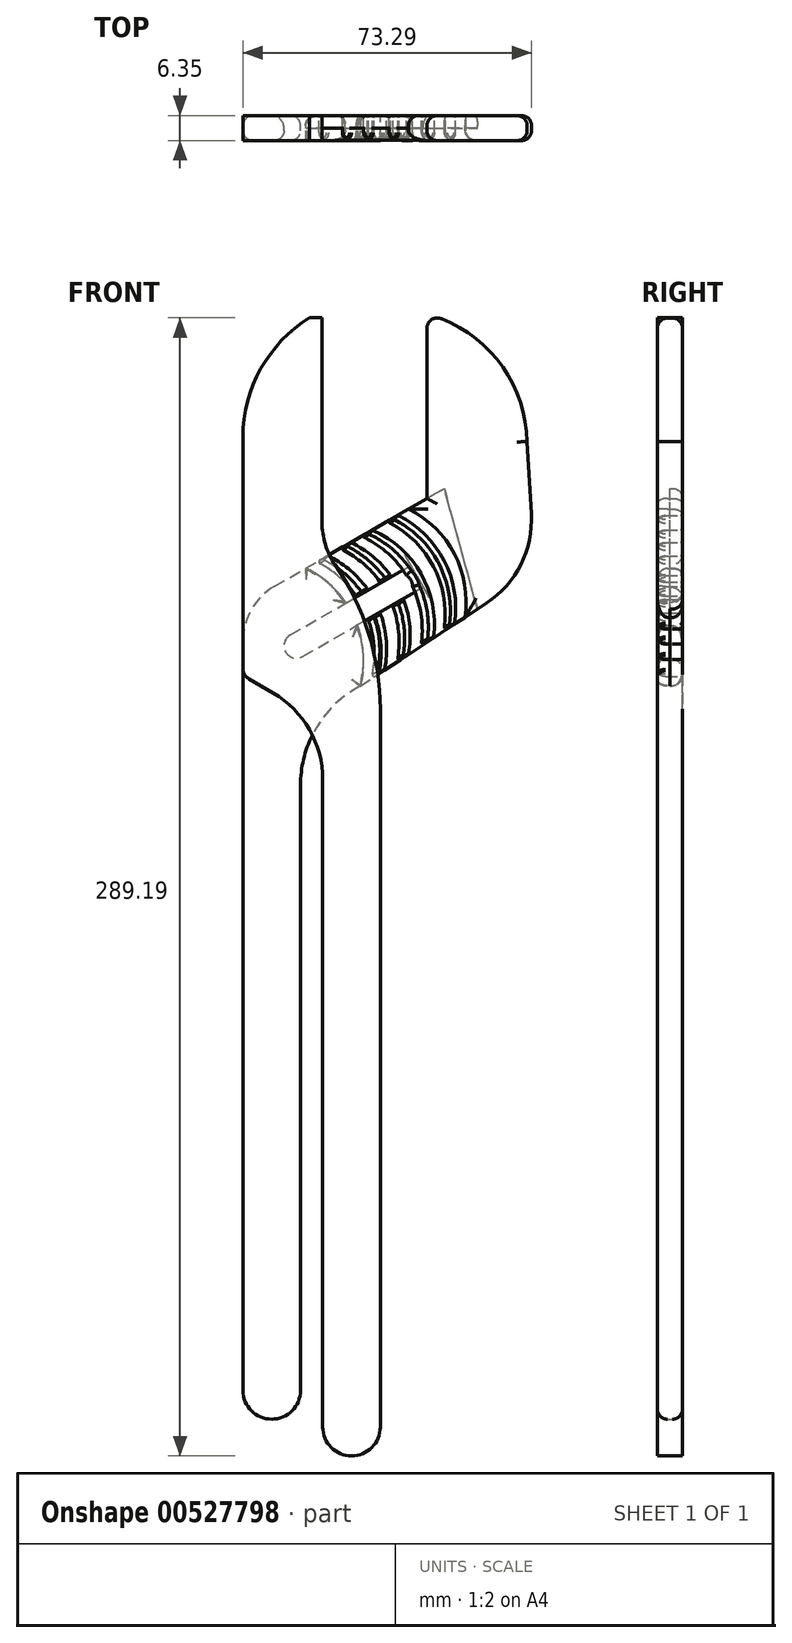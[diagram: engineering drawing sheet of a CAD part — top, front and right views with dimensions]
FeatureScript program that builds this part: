
annotation { "Feature Type Name" : "Feature", "Feature Type Description" : "" }
export const myFeature = defineFeature(function(context is Context, id is Id, definition is map)
    precondition{}
    {
        {
            var Q0;
            Q0=qCreatedBy(makeId("Front.planeOp"),FACE);
            var sketch = newSketch(context, id + "F0", { "sketchPlane" : qUnion([Q0])});
            skLineSegment(sketch, "E0", {"start": v(-2.94, 1.56) * mm, "end": v(-2.94, 179.72) * mm});
            skLineSegment(sketch, "E1", {"start": v(11.68, -10.78) * mm, "end": v(11.68, 143.04) * mm});
            skLineSegment(sketch, "E2", {"start": v(5, 193.46) * mm, "end": v(43.8, 215.87) * mm});
            skLineSegment(sketch, "E3", {"start": v(43.8, 261.68) * mm, "end": v(43.8, 215.87) * mm});
            skPoint(sketch, "E4.visualSharp", {"position": v(11.68, 160.66) * mm});
            skPoint(sketch, "E5.visualSharp", {"position": v(71.16, 197.3) * mm});
            skPoint(sketch, "E6.visualSharp", {"position": v(-2.94, 188.88) * mm});
            skArc(sketch, "E6.filletArc", {"start": v(5, 193.46) * mm, "mid": v(-0.82, 187.65) * mm, "end": v(-2.94, 179.72) * mm});
            skPoint(sketch, "E7.startSnap0", {"position": v(-0.82, 187.65) * mm});
            skLineSegment(sketch, "E8", {"start": v(-2.94, 1.56) * mm, "end": v(-2.94, -10.78) * mm});
            skLineSegment(sketch, "E9", {"start": v(26.87, 168.17) * mm, "end": v(58.9, 189.24) * mm});
            skArc(sketch, "E10", {"start": v(69.24, 230.28) * mm, "mid": v(62.94, 249.4) * mm, "end": v(46.97, 261.68) * mm});
            skLineSegment(sketch, "E11", {"start": v(43.8, 261.68) * mm, "end": v(46.97, 261.68) * mm});
            skLineSegment(sketch, "E12", {"start": v(69.24, 230.28) * mm, "end": v(70.3, 211.93) * mm});
            skArc(sketch, "E13.filletArc", {"start": v(58.9, 189.24) * mm, "mid": v(67.64, 199.06) * mm, "end": v(70.3, 211.93) * mm});
            skLineSegment(sketch, "E14", {"start": v(12.24, 175.65) * mm, "end": v(38.54, 190.84) * mm});
            skLineSegment(sketch, "E15", {"start": v(9.07, 181.15) * mm, "end": v(35.37, 196.34) * mm});
            skArc(sketch, "E16", {"start": v(-2.94, -10.78) * mm, "mid": v(4.37, -18.1) * mm, "end": v(11.68, -10.78) * mm});
            skArc(sketch, "E17", {"start": v(53.42, 185.63) * mm, "mid": v(50.77, 201.74) * mm, "end": v(39.08, 213.14) * mm});
            skArc(sketch, "E18", {"start": v(50.76, 183.88) * mm, "mid": v(48.13, 200.1) * mm, "end": v(36.33, 211.55) * mm});
            skArc(sketch, "E19", {"start": v(48.1, 182.14) * mm, "mid": v(45.48, 198.47) * mm, "end": v(33.58, 209.97) * mm});
            skArc(sketch, "E20", {"start": v(45.46, 180.4) * mm, "mid": v(42.28, 196.73) * mm, "end": v(29.9, 207.84) * mm});
            skArc(sketch, "E21", {"start": v(42.28, 178.3) * mm, "mid": v(42.34, 186.06) * mm, "end": v(40.13, 193.49) * mm});
            skPoint(sketch, "E21.startSnap0", {"position": v(42.28, 196.73) * mm});
            skArc(sketch, "E22", {"start": v(39.1, 176.22) * mm, "mid": v(39.42, 183.4) * mm, "end": v(37.77, 190.4) * mm});
            skArc(sketch, "E23", {"start": v(36.2, 174.3) * mm, "mid": v(36.62, 181.63) * mm, "end": v(35, 188.79) * mm});
            skArc(sketch, "E24", {"start": v(29.65, 170) * mm, "mid": v(30.36, 177.67) * mm, "end": v(28.8, 185.22) * mm});
            skArc(sketch, "E25", {"start": v(26.87, 168.17) * mm, "mid": v(27.65, 175.97) * mm, "end": v(26.08, 183.64) * mm});
            skArc(sketch, "E26", {"start": v(9.07, 181.15) * mm, "mid": v(7.9, 176.81) * mm, "end": v(12.24, 175.65) * mm});
            skArc(sketch, "E27", {"start": v(38.54, 190.84) * mm, "mid": v(39.7, 195.17) * mm, "end": v(35.37, 196.34) * mm});
            skArc(sketch, "E28.trimOffspring", {"start": v(23.18, 189.3) * mm, "mid": v(18.69, 194.37) * mm, "end": v(13.04, 198.11) * mm});
            skArc(sketch, "E29.trimOffspring", {"start": v(25.92, 190.88) * mm, "mid": v(21.43, 195.95) * mm, "end": v(15.8, 199.7) * mm});
            skArc(sketch, "E30.trimOffspring", {"start": v(32.02, 194.4) * mm, "mid": v(27.44, 199.44) * mm, "end": v(21.72, 203.12) * mm});
            skArc(sketch, "E31.trimOffspring", {"start": v(34.77, 196) * mm, "mid": v(30.16, 201.01) * mm, "end": v(24.4, 204.67) * mm});
            skArc(sketch, "E32.trimOffspring", {"start": v(38.6, 196.3) * mm, "mid": v(33.6, 202.13) * mm, "end": v(27.15, 206.25) * mm});
            skArc(sketch, "E33", {"start": v(32.99, 172.2) * mm, "mid": v(33.48, 179.66) * mm, "end": v(31.83, 186.96) * mm});
            skArc(sketch, "E34.trimOffspring", {"start": v(28.86, 192.58) * mm, "mid": v(24.27, 197.6) * mm, "end": v(18.54, 201.29) * mm});
            skArc(sketch, "E35", {"start": v(26.87, 168.17) * mm, "mid": v(15.77, 157.72) * mm, "end": v(11.68, 143.04) * mm});
            skSolve(sketch);
        }
        {
            var Q0;
            Q0=makeQuery(id+"F0.imprint","IMPRINT",FACE,{"disambiguationData":[TD([[makeQuery(id+"F0.imprint","IMPRINT",EDGE,{"derivedFrom":sQuery(id+"F0.wireOp",EDGE,"E0")}),-1.0]])]});
            var Q1;
            {var subQ0=sQuery(id+"F0.wireOp",EDGE,"E29.trimOffspring");Q1=makeQuery(id+"F0.imprint","IMPRINT",FACE,{"disambiguationData":[TD([[makeQuery(id+"F0.imprint","IMPRINT",EDGE,{"derivedFrom":subQ0}),-1.0]])]});}
            var Q2;
            {var subQ0=sQuery(id+"F0.wireOp",EDGE,"E30.trimOffspring");Q2=makeQuery(id+"F0.imprint","IMPRINT",FACE,{"disambiguationData":[TD([[makeQuery(id+"F0.imprint","IMPRINT",EDGE,{"derivedFrom":subQ0}),-1.0]])]});}
            var Q3;
            {var subQ1=sQuery(id+"F0.wireOp",EDGE,"E20");Q3=makeQuery(id+"F0.imprint","IMPRINT",FACE,{"disambiguationData":[TD([[makeQuery(id+"F0.imprint","IMPRINT",EDGE,{"derivedFrom":subQ1}),1.0]])]});}
            var Q4;
            {var subQ0=sQuery(id+"F0.wireOp",EDGE,"E18");Q4=makeQuery(id+"F0.imprint","IMPRINT",FACE,{"disambiguationData":[TD([[makeQuery(id+"F0.imprint","IMPRINT",EDGE,{"derivedFrom":subQ0}),1.0]])]});}
            var Q5;
            {var subQ3=sQuery(id+"F0.wireOp",EDGE,"E3");Q5=makeQuery(id+"F0.imprint","IMPRINT",FACE,{"disambiguationData":[TD([[makeQuery(id+"F0.imprint","IMPRINT",EDGE,{"derivedFrom":subQ3}),1.0]])]});}
            var Q6;
            {var subQ0=sQuery(id+"F0.wireOp",EDGE,"E24");Q6=makeQuery(id+"F0.imprint","IMPRINT",FACE,{"disambiguationData":[TD([[makeQuery(id+"F0.imprint","IMPRINT",EDGE,{"derivedFrom":subQ0}),-1.0]])]});}
            var Q7;
            {var subQ0=sQuery(id+"F0.wireOp",EDGE,"E22");Q7=makeQuery(id+"F0.imprint","IMPRINT",FACE,{"disambiguationData":[TD([[makeQuery(id+"F0.imprint","IMPRINT",EDGE,{"derivedFrom":subQ0}),1.0]])]});}
            extrude(context, id + "F1", {"entities" : qUnion([Q0, Q1, Q2, Q3, Q4, Q5, Q6, Q7]), "depth" : 6.35 * mm, "offsetDistance" : 25.4 * mm});
        }
        {
            var Q0;
            Q0=makeQuery(id+"F1.opExtrude","CAP_FACE",FACE,{"disambiguationData":[OSD([sQuery(id+"F0.wireOp",EDGE,"E0"),sQuery(id+"F0.wireOp",EDGE,"E1"),sQuery(id+"F0.wireOp",EDGE,"E2"),sQuery(id+"F0.wireOp",EDGE,"E6.filletArc"),sQuery(id+"F0.wireOp",EDGE,"E8"),sQuery(id+"F0.wireOp",EDGE,"E14"),sQuery(id+"F0.wireOp",EDGE,"E15"),sQuery(id+"F0.wireOp",EDGE,"E16"),sQuery(id+"F0.wireOp",EDGE,"E25"),sQuery(id+"F0.wireOp",EDGE,"E26"),sQuery(id+"F0.wireOp",EDGE,"E28.trimOffspring"),sQuery(id+"F0.wireOp",EDGE,"E35")])],"isStart":true});
            var sketch = newSketch(context, id + "F2", { "sketchPlane" : qUnion([Q0])});
            skLineSegment(sketch, "E36", {"start": v(-26.87, 168.17) * mm, "end": v(-19.28, 179.72) * mm});
            skLineSegment(sketch, "E37", {"start": v(-8.8, 195.66) * mm, "end": v(-48.19, 218.4) * mm});
            skLineSegment(sketch, "E38", {"start": v(-26.87, 168.17) * mm, "end": v(-56.63, 187.74) * mm});
            skLineSegment(sketch, "E39", {"start": v(-56.63, 187.74) * mm, "end": v(-48.19, 218.4) * mm});
            skLineSegment(sketch, "E40", {"start": v(-42.07, 192.87) * mm, "end": v(-19.28, 179.72) * mm});
            skLineSegment(sketch, "E41", {"start": v(-38.9, 198.37) * mm, "end": v(-15.79, 185.03) * mm});
            skLineSegment(sketch, "E42.trimOffspring", {"start": v(-15.79, 185.03) * mm, "end": v(-8.8, 195.66) * mm});
            skLineSegment(sketch, "E43", {"start": v(-42.07, 192.87) * mm, "end": v(-42.88, 193.34) * mm});
            skLineSegment(sketch, "E44", {"start": v(-42.88, 193.34) * mm, "end": v(-39.7, 198.84) * mm});
            skLineSegment(sketch, "E45", {"start": v(-38.9, 198.37) * mm, "end": v(-39.7, 198.84) * mm});
            skSolve(sketch);
        }
        {
            var Q0;
            Q0=makeQuery(id+"F1.opExtrude","CAP_EDGE",EDGE,{"disambiguationData":[OSD([sQuery(id+"F0.wireOp",EDGE,"E0"),sQuery(id+"F0.wireOp",EDGE,"E8")])],"isStart":false});
            var Q1;
            Q1=makeQuery(id+"F1.opExtrude","CAP_EDGE",EDGE,{"disambiguationData":[OSD([sQuery(id+"F0.wireOp",EDGE,"E6.filletArc")])],"isStart":false});
            var Q2;
            {var subQ0=sQuery(id+"F0.wireOp",EDGE,"E2");Q2=makeQuery(id+"F1.opExtrude","CAP_EDGE",EDGE,{"disambiguationData":[OSD([subQ0]),TDD([makeQuery(id+"F0.imprint","IMPRINT",EDGE,{"disambiguationData":[TD([[makeQuery(id+"F0.imprint","INTERSECT",VERTEX,{"derivedFrom":[subQ0,sQuery(id+"F0.wireOp",EDGE,"E6.filletArc")]}),-1.0]])],"derivedFrom":subQ0})])],"isStart":false});}
            var Q3;
            Q3=makeQuery(id+"F1.opExtrude","CAP_EDGE",EDGE,{"disambiguationData":[OSD([sQuery(id+"F0.wireOp",EDGE,"E6.filletArc")])],"isStart":true});
            var Q4;
            {var subQ0=sQuery(id+"F0.wireOp",EDGE,"E2");Q4=makeQuery(id+"F1.opExtrude","CAP_EDGE",EDGE,{"disambiguationData":[OSD([subQ0]),TDD([makeQuery(id+"F0.imprint","IMPRINT",EDGE,{"disambiguationData":[TD([[makeQuery(id+"F0.imprint","INTERSECT",VERTEX,{"derivedFrom":[subQ0,sQuery(id+"F0.wireOp",EDGE,"E6.filletArc")]}),-1.0]])],"derivedFrom":subQ0})])],"isStart":true});}
            var Q5;
            Q5=makeQuery(id+"F1.opExtrude","CAP_EDGE",EDGE,{"disambiguationData":[OSD([sQuery(id+"F0.wireOp",EDGE,"E0"),sQuery(id+"F0.wireOp",EDGE,"E8")])],"isStart":true});
            var Q6;
            Q6=makeQuery(id+"F1.opExtrude","CAP_EDGE",EDGE,{"disambiguationData":[OSD([sQuery(id+"F0.wireOp",EDGE,"E1")])],"isStart":true});
            var Q7;
            Q7=makeQuery(id+"F1.opExtrude","CAP_EDGE",EDGE,{"disambiguationData":[OSD([sQuery(id+"F0.wireOp",EDGE,"E1")])],"isStart":false});
            var Q8;
            Q8=makeQuery(id+"F1.opExtrude","CAP_EDGE",EDGE,{"disambiguationData":[OSD([sQuery(id+"F0.wireOp",EDGE,"E16")])],"isStart":false});
            var Q9;
            Q9=makeQuery(id+"F1.opExtrude","CAP_EDGE",EDGE,{"disambiguationData":[OSD([sQuery(id+"F0.wireOp",EDGE,"E16")])],"isStart":true});
            var Q10;
            Q10=makeQuery(id+"F1.opExtrude","CAP_FACE",FACE,{"disambiguationData":[OSD([sQuery(id+"F0.wireOp",EDGE,"E0"),sQuery(id+"F0.wireOp",EDGE,"E1"),sQuery(id+"F0.wireOp",EDGE,"E2"),sQuery(id+"F0.wireOp",EDGE,"E6.filletArc"),sQuery(id+"F0.wireOp",EDGE,"E8"),sQuery(id+"F0.wireOp",EDGE,"E14"),sQuery(id+"F0.wireOp",EDGE,"E15"),sQuery(id+"F0.wireOp",EDGE,"E16"),sQuery(id+"F0.wireOp",EDGE,"E25"),sQuery(id+"F0.wireOp",EDGE,"E26"),sQuery(id+"F0.wireOp",EDGE,"E28.trimOffspring"),sQuery(id+"F0.wireOp",EDGE,"E35")])],"isStart":false});
            var Q11;
            Q11=makeQuery(id+"F1.opExtrude","CAP_EDGE",EDGE,{"disambiguationData":[OSD([sQuery(id+"F0.wireOp",EDGE,"E35")])],"isStart":true});
            fillet(context, id + "F3", {"entities" : qUnion([Q0, Q1, Q2, Q3, Q4, Q5, Q6, Q7, Q8, Q9, Q10, Q11]), "radius" : 2.54 * mm, "tangentPropagation" : true, "allowEdgeOverflow" : false});
        }
        {
            var Q0;
            Q0=makeQuery(id+"F1.opExtrude","CAP_EDGE",EDGE,{"disambiguationData":[OSD([sQuery(id+"F0.wireOp",EDGE,"E24")])],"isStart":false});
            var Q1;
            Q1=makeQuery(id+"F1.opExtrude","CAP_EDGE",EDGE,{"disambiguationData":[OSD([sQuery(id+"F0.wireOp",EDGE,"E33")])],"isStart":false});
            var Q2;
            Q2=makeQuery(id+"F1.opExtrude","CAP_EDGE",EDGE,{"disambiguationData":[OSD([sQuery(id+"F0.wireOp",EDGE,"E23")])],"isStart":false});
            var Q3;
            Q3=makeQuery(id+"F1.opExtrude","CAP_EDGE",EDGE,{"disambiguationData":[OSD([sQuery(id+"F0.wireOp",EDGE,"E22")])],"isStart":false});
            var Q4;
            Q4=makeQuery(id+"F1.opExtrude","CAP_EDGE",EDGE,{"disambiguationData":[OSD([sQuery(id+"F0.wireOp",EDGE,"E29.trimOffspring")])],"isStart":false});
            var Q5;
            Q5=makeQuery(id+"F1.opExtrude","CAP_EDGE",EDGE,{"disambiguationData":[OSD([sQuery(id+"F0.wireOp",EDGE,"E30.trimOffspring")])],"isStart":false});
            var Q6;
            Q6=makeQuery(id+"F1.opExtrude","CAP_EDGE",EDGE,{"disambiguationData":[OSD([sQuery(id+"F0.wireOp",EDGE,"E19")])],"isStart":false});
            var Q7;
            Q7=makeQuery(id+"F1.opExtrude","CAP_EDGE",EDGE,{"disambiguationData":[OSD([sQuery(id+"F0.wireOp",EDGE,"E18")])],"isStart":false});
            var Q8;
            Q8=makeQuery(id+"F1.opExtrude","CAP_EDGE",EDGE,{"disambiguationData":[OSD([sQuery(id+"F0.wireOp",EDGE,"E20")])],"isStart":false});
            var Q9;
            Q9=makeQuery(id+"F1.opExtrude","CAP_EDGE",EDGE,{"disambiguationData":[OSD([sQuery(id+"F0.wireOp",EDGE,"E27")])],"isStart":false});
            var Q10;
            Q10=makeQuery(id+"F1.opExtrude","CAP_EDGE",EDGE,{"disambiguationData":[OSD([sQuery(id+"F0.wireOp",EDGE,"E32.trimOffspring")])],"isStart":false});
            var Q11;
            Q11=makeQuery(id+"F1.opExtrude","CAP_EDGE",EDGE,{"disambiguationData":[OSD([sQuery(id+"F0.wireOp",EDGE,"E21")])],"isStart":false});
            var Q12;
            Q12=makeQuery(id+"F1.opExtrude","CAP_EDGE",EDGE,{"disambiguationData":[OSD([sQuery(id+"F0.wireOp",EDGE,"E31.trimOffspring")])],"isStart":false});
            var Q13;
            Q13=makeQuery(id+"F1.opExtrude","CAP_EDGE",EDGE,{"disambiguationData":[OSD([sQuery(id+"F0.wireOp",EDGE,"E34.trimOffspring")])],"isStart":false});
            fillet(context, id + "F4", {"entities" : qUnion([Q0, Q1, Q2, Q3, Q4, Q5, Q6, Q7, Q8, Q9, Q10, Q11, Q12, Q13]), "radius" : 2.03 * mm, "tangentPropagation" : true, "allowEdgeOverflow" : false});
        }
        {
            var Q0;
            Q0=makeQuery(id+"FH2u4R809bOaR1E_8.opExtrude","CAP_EDGE",EDGE,{"disambiguationData":[OSD([sQuery(id+"F2.wireOp",EDGE,"E38")])],"isStart":true});
            var Q1;
            Q1=makeQuery(id+"FH2u4R809bOaR1E_8.opExtrude","CAP_EDGE",EDGE,{"disambiguationData":[OSD([sQuery(id+"F2.wireOp",EDGE,"E38")])],"isStart":false});
            var Q2;
            {var subQ0=sQuery(id+"F0.wireOp",EDGE,"E9");Q2=makeQuery(id+"F1.opExtrude","CAP_EDGE",EDGE,{"disambiguationData":[OSD([subQ0]),TDD([makeQuery(id+"F0.imprint","IMPRINT",EDGE,{"disambiguationData":[TD([[makeQuery(id+"F0.imprint","INTERSECT",VERTEX,{"derivedFrom":[subQ0,sQuery(id+"F0.wireOp",EDGE,"E13.filletArc")]}),1.0]])],"derivedFrom":subQ0})])],"isStart":true});}
            var Q3;
            Q3=makeQuery(id+"F1.opExtrude","CAP_EDGE",EDGE,{"disambiguationData":[OSD([sQuery(id+"F0.wireOp",EDGE,"E13.filletArc")])],"isStart":false});
            var Q4;
            {var subQ0=sQuery(id+"F0.wireOp",EDGE,"E9");Q4=makeQuery(id+"F1.opExtrude","CAP_EDGE",EDGE,{"disambiguationData":[OSD([subQ0]),TDD([makeQuery(id+"F0.imprint","IMPRINT",EDGE,{"disambiguationData":[TD([[makeQuery(id+"F0.imprint","INTERSECT",VERTEX,{"derivedFrom":[subQ0,sQuery(id+"F0.wireOp",EDGE,"E13.filletArc")]}),1.0]])],"derivedFrom":subQ0})])],"isStart":false});}
            var Q5;
            Q5=makeQuery(id+"F1.opExtrude","CAP_EDGE",EDGE,{"disambiguationData":[OSD([sQuery(id+"F0.wireOp",EDGE,"E17")])],"isStart":false});
            var Q6;
            {var subQ0=sQuery(id+"F0.wireOp",EDGE,"E2");Q6=makeQuery(id+"F1.opExtrude","CAP_EDGE",EDGE,{"disambiguationData":[OSD([subQ0]),TDD([makeQuery(id+"F0.imprint","IMPRINT",EDGE,{"disambiguationData":[TD([[makeQuery(id+"F0.imprint","INTERSECT",VERTEX,{"derivedFrom":[subQ0,sQuery(id+"F0.wireOp",EDGE,"E3")]}),1.0]])],"derivedFrom":subQ0})])],"isStart":false});}
            var Q7;
            Q7=makeQuery(id+"F1.opExtrude","CAP_EDGE",EDGE,{"disambiguationData":[OSD([sQuery(id+"F0.wireOp",EDGE,"E3")])],"isStart":false});
            var Q8;
            Q8=makeQuery(id+"F1.opExtrude","CAP_EDGE",EDGE,{"disambiguationData":[OSD([sQuery(id+"F0.wireOp",EDGE,"E10")])],"isStart":false});
            var Q9;
            Q9=makeQuery(id+"F1.opExtrude","CAP_EDGE",EDGE,{"disambiguationData":[OSD([sQuery(id+"F0.wireOp",EDGE,"E10")])],"isStart":true});
            var Q10;
            Q10=makeQuery(id+"F1.opExtrude","CAP_EDGE",EDGE,{"disambiguationData":[OSD([sQuery(id+"F0.wireOp",EDGE,"E12")])],"isStart":false});
            var Q11;
            Q11=makeQuery(id+"F1.opExtrude","SWEPT_EDGE",EDGE,{"disambiguationData":[OSD([sQuery(id+"F0.wireOp",EDGE,"E10"),sQuery(id+"F0.wireOp",EDGE,"E11")])]});
            var Q12;
            Q12=makeQuery(id+"F1.opExtrude","SWEPT_EDGE",EDGE,{"disambiguationData":[OSD([sQuery(id+"F0.wireOp",EDGE,"E3"),sQuery(id+"F0.wireOp",EDGE,"E11")])]});
            var Q13;
            Q13=makeQuery(id+"F1.opExtrude","CAP_EDGE",EDGE,{"disambiguationData":[OSD([sQuery(id+"F0.wireOp",EDGE,"E11")])],"isStart":true});
            var Q14;
            Q14=makeQuery(id+"F1.opExtrude","CAP_EDGE",EDGE,{"disambiguationData":[OSD([sQuery(id+"F0.wireOp",EDGE,"E11")])],"isStart":false});
            var Q15;
            Q15=makeQuery(id+"FH2u4R809bOaR1E_8.opExtrude","CAP_EDGE",EDGE,{"disambiguationData":[OSD([sQuery(id+"F2.wireOp",EDGE,"E37")])],"isStart":false});
            var Q16;
            Q16=makeQuery(id+"FH2u4R809bOaR1E_8.opExtrude","CAP_EDGE",EDGE,{"disambiguationData":[OSD([sQuery(id+"F2.wireOp",EDGE,"E37")])],"isStart":true});
            var Q17;
            Q17=makeQuery(id+"F1.opExtrude","CAP_EDGE",EDGE,{"disambiguationData":[OSD([sQuery(id+"F0.wireOp",EDGE,"E3")])],"isStart":true});
            fillet(context, id + "F5", {"entities" : qUnion([Q0, Q1, Q2, Q3, Q4, Q5, Q6, Q7, Q8, Q9, Q10, Q11, Q12, Q13, Q14, Q15, Q16, Q17]), "radius" : 2.54 * mm, "tangentPropagation" : true, "allowEdgeOverflow" : false});
        }
        {
            var Q0;
            {var subQ0=sQuery(id+"F0.wireOp",EDGE,"E2");var subQ1=sQuery(id+"F0.wireOp",EDGE,"E19");Q0=makeQuery(id+"F4.opFillet","BLEND_EDGE",EDGE,{"blendedFrom":[makeQuery(id+"F1.opExtrude","CAP_EDGE",EDGE,{"disambiguationData":[OSD([subQ1])],"isStart":false}),makeQuery(id+"F1.opExtrude","SWEPT_FACE",FACE,{"disambiguationData":[OSD([subQ0]),TDD([makeQuery(id+"F0.imprint","IMPRINT",EDGE,{"disambiguationData":[TD([[makeQuery(id+"F0.imprint","INTERSECT",VERTEX,{"derivedFrom":[subQ0,sQuery(id+"F0.wireOp",EDGE,"E18")]}),1.0]])],"derivedFrom":subQ0})])]})],"blendedInto":[makeQuery(id+"F1.opExtrude","SWEPT_FACE",FACE,{"disambiguationData":[OSD([subQ0]),TDD([makeQuery(id+"F0.imprint","IMPRINT",EDGE,{"disambiguationData":[TD([[makeQuery(id+"F0.imprint","INTERSECT",VERTEX,{"derivedFrom":[subQ0,sQuery(id+"F0.wireOp",EDGE,"E18")]}),1.0]])],"derivedFrom":subQ0})])]})]});}
            var Q1;
            {var subQ0=sQuery(id+"F0.wireOp",EDGE,"E18");var subQ1=sQuery(id+"F0.wireOp",EDGE,"E2");Q1=makeQuery(id+"F4.opFillet","BLEND_EDGE",EDGE,{"blendedFrom":[makeQuery(id+"F1.opExtrude","CAP_EDGE",EDGE,{"disambiguationData":[OSD([subQ0])],"isStart":false}),makeQuery(id+"F1.opExtrude","SWEPT_FACE",FACE,{"disambiguationData":[OSD([subQ1]),TDD([makeQuery(id+"F0.imprint","IMPRINT",EDGE,{"disambiguationData":[TD([[makeQuery(id+"F0.imprint","INTERSECT",VERTEX,{"derivedFrom":[subQ1,subQ0]}),1.0]])],"derivedFrom":subQ1})])]})],"blendedInto":[makeQuery(id+"F1.opExtrude","SWEPT_FACE",FACE,{"disambiguationData":[OSD([subQ1]),TDD([makeQuery(id+"F0.imprint","IMPRINT",EDGE,{"disambiguationData":[TD([[makeQuery(id+"F0.imprint","INTERSECT",VERTEX,{"derivedFrom":[subQ1,subQ0]}),1.0]])],"derivedFrom":subQ1})])]})]});}
            var Q2;
            {var subQ0=sQuery(id+"F0.wireOp",EDGE,"E2");Q2=makeQuery(id+"F1.opExtrude","CAP_EDGE",EDGE,{"disambiguationData":[OSD([subQ0]),TDD([makeQuery(id+"F0.imprint","IMPRINT",EDGE,{"disambiguationData":[TD([[makeQuery(id+"F0.imprint","INTERSECT",VERTEX,{"derivedFrom":[subQ0,sQuery(id+"F0.wireOp",EDGE,"E18")]}),1.0]])],"derivedFrom":subQ0})])],"isStart":true});}
            var Q3;
            Q3=makeQuery(id+"F1.opExtrude","SWEPT_EDGE",EDGE,{"disambiguationData":[OSD([sQuery(id+"F0.wireOp",EDGE,"E2"),sQuery(id+"F0.wireOp",EDGE,"E18")])]});
            var Q4;
            Q4=makeQuery(id+"F1.opExtrude","SWEPT_EDGE",EDGE,{"disambiguationData":[OSD([sQuery(id+"F0.wireOp",EDGE,"E2"),sQuery(id+"F0.wireOp",EDGE,"E19")])]});
            var Q5;
            Q5=makeQuery(id+"F1.opExtrude","CAP_EDGE",EDGE,{"disambiguationData":[OSD([sQuery(id+"F0.wireOp",EDGE,"E18")])],"isStart":true});
            var Q6;
            Q6=makeQuery(id+"F1.opExtrude","CAP_EDGE",EDGE,{"disambiguationData":[OSD([sQuery(id+"F0.wireOp",EDGE,"E19")])],"isStart":true});
            var Q7;
            Q7=makeQuery(id+"F1.opExtrude","CAP_EDGE",EDGE,{"disambiguationData":[OSD([sQuery(id+"F0.wireOp",EDGE,"E20")])],"isStart":true});
            var Q8;
            {var subQ0=sQuery(id+"F0.wireOp",EDGE,"E2");Q8=makeQuery(id+"F1.opExtrude","CAP_EDGE",EDGE,{"disambiguationData":[OSD([subQ0]),TDD([makeQuery(id+"F0.imprint","IMPRINT",EDGE,{"disambiguationData":[TD([[makeQuery(id+"F0.imprint","INTERSECT",VERTEX,{"derivedFrom":[subQ0,sQuery(id+"F0.wireOp",EDGE,"E20")]}),1.0]])],"derivedFrom":subQ0})])],"isStart":true});}
            var Q9;
            Q9=makeQuery(id+"F1.opExtrude","SWEPT_EDGE",EDGE,{"disambiguationData":[OSD([sQuery(id+"F0.wireOp",EDGE,"E2"),sQuery(id+"F0.wireOp",EDGE,"E20")])]});
            var Q10;
            Q10=makeQuery(id+"F1.opExtrude","SWEPT_EDGE",EDGE,{"disambiguationData":[OSD([sQuery(id+"F0.wireOp",EDGE,"E2"),sQuery(id+"F0.wireOp",EDGE,"E32.trimOffspring")])]});
            var Q11;
            Q11=makeQuery(id+"F1.opExtrude","CAP_EDGE",EDGE,{"disambiguationData":[OSD([sQuery(id+"F0.wireOp",EDGE,"E32.trimOffspring")])],"isStart":true});
            var Q12;
            Q12=makeQuery(id+"F1.opExtrude","CAP_EDGE",EDGE,{"disambiguationData":[OSD([sQuery(id+"F0.wireOp",EDGE,"E27")])],"isStart":true});
            var Q13;
            {var subQ0=sQuery(id+"F0.wireOp",EDGE,"E2");var subQ1=sQuery(id+"F0.wireOp",EDGE,"E32.trimOffspring");Q13=makeQuery(id+"F4.opFillet","BLEND_EDGE",EDGE,{"blendedFrom":[makeQuery(id+"F1.opExtrude","CAP_EDGE",EDGE,{"disambiguationData":[OSD([subQ1])],"isStart":false}),makeQuery(id+"F1.opExtrude","SWEPT_FACE",FACE,{"disambiguationData":[OSD([subQ0]),TDD([makeQuery(id+"F0.imprint","IMPRINT",EDGE,{"disambiguationData":[TD([[makeQuery(id+"F0.imprint","INTERSECT",VERTEX,{"derivedFrom":[subQ0,sQuery(id+"F0.wireOp",EDGE,"E20")]}),1.0]])],"derivedFrom":subQ0})])]})],"blendedInto":[makeQuery(id+"F1.opExtrude","SWEPT_FACE",FACE,{"disambiguationData":[OSD([subQ0]),TDD([makeQuery(id+"F0.imprint","IMPRINT",EDGE,{"disambiguationData":[TD([[makeQuery(id+"F0.imprint","INTERSECT",VERTEX,{"derivedFrom":[subQ0,sQuery(id+"F0.wireOp",EDGE,"E20")]}),1.0]])],"derivedFrom":subQ0})])]})]});}
            var Q14;
            {var subQ0=sQuery(id+"F0.wireOp",EDGE,"E20");var subQ1=sQuery(id+"F0.wireOp",EDGE,"E2");Q14=makeQuery(id+"F4.opFillet","BLEND_EDGE",EDGE,{"blendedFrom":[makeQuery(id+"F1.opExtrude","CAP_EDGE",EDGE,{"disambiguationData":[OSD([subQ0])],"isStart":false}),makeQuery(id+"F1.opExtrude","SWEPT_FACE",FACE,{"disambiguationData":[OSD([subQ1]),TDD([makeQuery(id+"F0.imprint","IMPRINT",EDGE,{"disambiguationData":[TD([[makeQuery(id+"F0.imprint","INTERSECT",VERTEX,{"derivedFrom":[subQ1,subQ0]}),1.0]])],"derivedFrom":subQ1})])]})],"blendedInto":[makeQuery(id+"F1.opExtrude","SWEPT_FACE",FACE,{"disambiguationData":[OSD([subQ1]),TDD([makeQuery(id+"F0.imprint","IMPRINT",EDGE,{"disambiguationData":[TD([[makeQuery(id+"F0.imprint","INTERSECT",VERTEX,{"derivedFrom":[subQ1,subQ0]}),1.0]])],"derivedFrom":subQ1})])]})]});}
            var Q15;
            Q15=makeQuery(id+"F1.opExtrude","SWEPT_EDGE",EDGE,{"disambiguationData":[OSD([sQuery(id+"F0.wireOp",EDGE,"E2"),sQuery(id+"F0.wireOp",EDGE,"E31.trimOffspring")])]});
            var Q16;
            {var subQ0=sQuery(id+"F0.wireOp",EDGE,"E2");var subQ1=sQuery(id+"F0.wireOp",EDGE,"E31.trimOffspring");Q16=makeQuery(id+"F4.opFillet","BLEND_EDGE",EDGE,{"blendedFrom":[makeQuery(id+"F1.opExtrude","CAP_EDGE",EDGE,{"disambiguationData":[OSD([subQ1])],"isStart":false}),makeQuery(id+"F1.opExtrude","SWEPT_FACE",FACE,{"disambiguationData":[OSD([subQ0]),TDD([makeQuery(id+"F0.imprint","IMPRINT",EDGE,{"disambiguationData":[TD([[makeQuery(id+"F0.imprint","INTERSECT",VERTEX,{"derivedFrom":[subQ0,sQuery(id+"F0.wireOp",EDGE,"E30.trimOffspring")]}),-1.0]])],"derivedFrom":subQ0})])]})],"blendedInto":[makeQuery(id+"F1.opExtrude","SWEPT_FACE",FACE,{"disambiguationData":[OSD([subQ0]),TDD([makeQuery(id+"F0.imprint","IMPRINT",EDGE,{"disambiguationData":[TD([[makeQuery(id+"F0.imprint","INTERSECT",VERTEX,{"derivedFrom":[subQ0,sQuery(id+"F0.wireOp",EDGE,"E30.trimOffspring")]}),-1.0]])],"derivedFrom":subQ0})])]})]});}
            var Q17;
            Q17=makeQuery(id+"F1.opExtrude","CAP_EDGE",EDGE,{"disambiguationData":[OSD([sQuery(id+"F0.wireOp",EDGE,"E31.trimOffspring")])],"isStart":true});
            var Q18;
            Q18=makeQuery(id+"F1.opExtrude","SWEPT_EDGE",EDGE,{"disambiguationData":[OSD([sQuery(id+"F0.wireOp",EDGE,"E2"),sQuery(id+"F0.wireOp",EDGE,"E30.trimOffspring")])]});
            var Q19;
            {var subQ0=sQuery(id+"F0.wireOp",EDGE,"E2");Q19=makeQuery(id+"F1.opExtrude","CAP_EDGE",EDGE,{"disambiguationData":[OSD([subQ0]),TDD([makeQuery(id+"F0.imprint","IMPRINT",EDGE,{"disambiguationData":[TD([[makeQuery(id+"F0.imprint","INTERSECT",VERTEX,{"derivedFrom":[subQ0,sQuery(id+"F0.wireOp",EDGE,"E30.trimOffspring")]}),-1.0]])],"derivedFrom":subQ0})])],"isStart":true});}
            var Q20;
            Q20=makeQuery(id+"F1.opExtrude","CAP_EDGE",EDGE,{"disambiguationData":[OSD([sQuery(id+"F0.wireOp",EDGE,"E30.trimOffspring")])],"isStart":true});
            var Q21;
            {var subQ0=sQuery(id+"F0.wireOp",EDGE,"E15");Q21=makeQuery(id+"F1.opExtrude","CAP_EDGE",EDGE,{"disambiguationData":[OSD([subQ0]),TDD([makeQuery(id+"F0.imprint","IMPRINT",EDGE,{"disambiguationData":[TD([[makeQuery(id+"F0.imprint","INTERSECT",VERTEX,{"derivedFrom":[subQ0,sQuery(id+"F0.wireOp",EDGE,"E30.trimOffspring")]}),-1.0]])],"derivedFrom":subQ0})])],"isStart":true});}
            var Q22;
            {var subQ0=sQuery(id+"F0.wireOp",EDGE,"E30.trimOffspring");var subQ1=sQuery(id+"F0.wireOp",EDGE,"E2");Q22=makeQuery(id+"F4.opFillet","BLEND_EDGE",EDGE,{"blendedFrom":[makeQuery(id+"F1.opExtrude","CAP_EDGE",EDGE,{"disambiguationData":[OSD([subQ0])],"isStart":false}),makeQuery(id+"F1.opExtrude","SWEPT_FACE",FACE,{"disambiguationData":[OSD([subQ1]),TDD([makeQuery(id+"F0.imprint","IMPRINT",EDGE,{"disambiguationData":[TD([[makeQuery(id+"F0.imprint","INTERSECT",VERTEX,{"derivedFrom":[subQ1,subQ0]}),-1.0]])],"derivedFrom":subQ1})])]})],"blendedInto":[makeQuery(id+"F1.opExtrude","SWEPT_FACE",FACE,{"disambiguationData":[OSD([subQ1]),TDD([makeQuery(id+"F0.imprint","IMPRINT",EDGE,{"disambiguationData":[TD([[makeQuery(id+"F0.imprint","INTERSECT",VERTEX,{"derivedFrom":[subQ1,subQ0]}),-1.0]])],"derivedFrom":subQ1})])]})]});}
            var Q23;
            {var subQ0=sQuery(id+"F0.wireOp",EDGE,"E2");var subQ1=sQuery(id+"F0.wireOp",EDGE,"E34.trimOffspring");Q23=makeQuery(id+"F4.opFillet","BLEND_EDGE",EDGE,{"blendedFrom":[makeQuery(id+"F1.opExtrude","CAP_EDGE",EDGE,{"disambiguationData":[OSD([subQ1])],"isStart":false}),makeQuery(id+"F1.opExtrude","SWEPT_FACE",FACE,{"disambiguationData":[OSD([subQ0]),TDD([makeQuery(id+"F0.imprint","IMPRINT",EDGE,{"disambiguationData":[TD([[makeQuery(id+"F0.imprint","INTERSECT",VERTEX,{"derivedFrom":[subQ0,sQuery(id+"F0.wireOp",EDGE,"E29.trimOffspring")]}),-1.0]])],"derivedFrom":subQ0})])]})],"blendedInto":[makeQuery(id+"F1.opExtrude","SWEPT_FACE",FACE,{"disambiguationData":[OSD([subQ0]),TDD([makeQuery(id+"F0.imprint","IMPRINT",EDGE,{"disambiguationData":[TD([[makeQuery(id+"F0.imprint","INTERSECT",VERTEX,{"derivedFrom":[subQ0,sQuery(id+"F0.wireOp",EDGE,"E29.trimOffspring")]}),-1.0]])],"derivedFrom":subQ0})])]})]});}
            var Q24;
            {var subQ0=sQuery(id+"F0.wireOp",EDGE,"E29.trimOffspring");var subQ1=sQuery(id+"F0.wireOp",EDGE,"E2");Q24=makeQuery(id+"F4.opFillet","BLEND_EDGE",EDGE,{"blendedFrom":[makeQuery(id+"F1.opExtrude","CAP_EDGE",EDGE,{"disambiguationData":[OSD([subQ0])],"isStart":false}),makeQuery(id+"F1.opExtrude","SWEPT_FACE",FACE,{"disambiguationData":[OSD([subQ1]),TDD([makeQuery(id+"F0.imprint","IMPRINT",EDGE,{"disambiguationData":[TD([[makeQuery(id+"F0.imprint","INTERSECT",VERTEX,{"derivedFrom":[subQ1,subQ0]}),-1.0]])],"derivedFrom":subQ1})])]})],"blendedInto":[makeQuery(id+"F1.opExtrude","SWEPT_FACE",FACE,{"disambiguationData":[OSD([subQ1]),TDD([makeQuery(id+"F0.imprint","IMPRINT",EDGE,{"disambiguationData":[TD([[makeQuery(id+"F0.imprint","INTERSECT",VERTEX,{"derivedFrom":[subQ1,subQ0]}),-1.0]])],"derivedFrom":subQ1})])]})]});}
            var Q25;
            Q25=makeQuery(id+"F1.opExtrude","SWEPT_EDGE",EDGE,{"disambiguationData":[OSD([sQuery(id+"F0.wireOp",EDGE,"E2"),sQuery(id+"F0.wireOp",EDGE,"E29.trimOffspring")])]});
            var Q26;
            Q26=makeQuery(id+"F1.opExtrude","SWEPT_EDGE",EDGE,{"disambiguationData":[OSD([sQuery(id+"F0.wireOp",EDGE,"E2"),sQuery(id+"F0.wireOp",EDGE,"E34.trimOffspring")])]});
            var Q27;
            {var subQ0=sQuery(id+"F0.wireOp",EDGE,"E2");Q27=makeQuery(id+"F1.opExtrude","CAP_EDGE",EDGE,{"disambiguationData":[OSD([subQ0]),TDD([makeQuery(id+"F0.imprint","IMPRINT",EDGE,{"disambiguationData":[TD([[makeQuery(id+"F0.imprint","INTERSECT",VERTEX,{"derivedFrom":[subQ0,sQuery(id+"F0.wireOp",EDGE,"E29.trimOffspring")]}),-1.0]])],"derivedFrom":subQ0})])],"isStart":true});}
            var Q28;
            Q28=makeQuery(id+"F1.opExtrude","CAP_EDGE",EDGE,{"disambiguationData":[OSD([sQuery(id+"F0.wireOp",EDGE,"E29.trimOffspring")])],"isStart":true});
            var Q29;
            {var subQ0=sQuery(id+"F0.wireOp",EDGE,"E15");Q29=makeQuery(id+"F1.opExtrude","CAP_EDGE",EDGE,{"disambiguationData":[OSD([subQ0]),TDD([makeQuery(id+"F0.imprint","IMPRINT",EDGE,{"disambiguationData":[TD([[makeQuery(id+"F0.imprint","INTERSECT",VERTEX,{"derivedFrom":[subQ0,sQuery(id+"F0.wireOp",EDGE,"E29.trimOffspring")]}),-1.0]])],"derivedFrom":subQ0})])],"isStart":true});}
            var Q30;
            Q30=makeQuery(id+"F1.opExtrude","CAP_EDGE",EDGE,{"disambiguationData":[OSD([sQuery(id+"F0.wireOp",EDGE,"E34.trimOffspring")])],"isStart":true});
            var Q31;
            {var subQ0=sQuery(id+"F0.wireOp",EDGE,"E14");Q31=makeQuery(id+"F1.opExtrude","CAP_EDGE",EDGE,{"disambiguationData":[OSD([subQ0]),TDD([makeQuery(id+"F0.imprint","IMPRINT",EDGE,{"disambiguationData":[TD([[makeQuery(id+"F0.imprint","INTERSECT",VERTEX,{"derivedFrom":[subQ0,sQuery(id+"F0.wireOp",EDGE,"E22")]}),1.0]])],"derivedFrom":subQ0})])],"isStart":true});}
            var Q32;
            Q32=makeQuery(id+"F1.opExtrude","CAP_EDGE",EDGE,{"disambiguationData":[OSD([sQuery(id+"F0.wireOp",EDGE,"E23")])],"isStart":true});
            var Q33;
            Q33=makeQuery(id+"F1.opExtrude","CAP_EDGE",EDGE,{"disambiguationData":[OSD([sQuery(id+"F0.wireOp",EDGE,"E21")])],"isStart":true});
            var Q34;
            Q34=makeQuery(id+"F1.opExtrude","CAP_EDGE",EDGE,{"disambiguationData":[OSD([sQuery(id+"F0.wireOp",EDGE,"E22")])],"isStart":true});
            var Q35;
            {var subQ0=sQuery(id+"F0.wireOp",EDGE,"E14");Q35=makeQuery(id+"F1.opExtrude","CAP_EDGE",EDGE,{"disambiguationData":[OSD([subQ0]),TDD([makeQuery(id+"F0.imprint","IMPRINT",EDGE,{"disambiguationData":[TD([[makeQuery(id+"F0.imprint","INTERSECT",VERTEX,{"derivedFrom":[subQ0,sQuery(id+"F0.wireOp",EDGE,"E24")]}),-1.0]])],"derivedFrom":subQ0})])],"isStart":true});}
            var Q36;
            Q36=makeQuery(id+"F1.opExtrude","CAP_EDGE",EDGE,{"disambiguationData":[OSD([sQuery(id+"F0.wireOp",EDGE,"E24")])],"isStart":true});
            var Q37;
            Q37=makeQuery(id+"F1.opExtrude","CAP_EDGE",EDGE,{"disambiguationData":[OSD([sQuery(id+"F0.wireOp",EDGE,"E33")])],"isStart":true});
            var Q38;
            {var subQ0=sQuery(id+"F0.wireOp",EDGE,"E18");var subQ1=sQuery(id+"F0.wireOp",EDGE,"E9");Q38=makeQuery(id+"F4.opFillet","BLEND_EDGE",EDGE,{"blendedFrom":[makeQuery(id+"F1.opExtrude","CAP_EDGE",EDGE,{"disambiguationData":[OSD([subQ0])],"isStart":false}),makeQuery(id+"F1.opExtrude","SWEPT_FACE",FACE,{"disambiguationData":[OSD([subQ1]),TDD([makeQuery(id+"F0.imprint","IMPRINT",EDGE,{"disambiguationData":[TD([[makeQuery(id+"F0.imprint","INTERSECT",VERTEX,{"derivedFrom":[subQ1,subQ0]}),1.0]])],"derivedFrom":subQ1})])]})],"blendedInto":[makeQuery(id+"F1.opExtrude","SWEPT_FACE",FACE,{"disambiguationData":[OSD([subQ1]),TDD([makeQuery(id+"F0.imprint","IMPRINT",EDGE,{"disambiguationData":[TD([[makeQuery(id+"F0.imprint","INTERSECT",VERTEX,{"derivedFrom":[subQ1,subQ0]}),1.0]])],"derivedFrom":subQ1})])]})]});}
            var Q39;
            Q39=makeQuery(id+"F1.opExtrude","SWEPT_EDGE",EDGE,{"disambiguationData":[OSD([sQuery(id+"F0.wireOp",EDGE,"E9"),sQuery(id+"F0.wireOp",EDGE,"E18")])]});
            var Q40;
            Q40=makeQuery(id+"F1.opExtrude","SWEPT_EDGE",EDGE,{"disambiguationData":[OSD([sQuery(id+"F0.wireOp",EDGE,"E9"),sQuery(id+"F0.wireOp",EDGE,"E19")])]});
            var Q41;
            {var subQ0=sQuery(id+"F0.wireOp",EDGE,"E9");var subQ1=sQuery(id+"F0.wireOp",EDGE,"E21");Q41=makeQuery(id+"F4.opFillet","BLEND_EDGE",EDGE,{"blendedFrom":[makeQuery(id+"F1.opExtrude","CAP_EDGE",EDGE,{"disambiguationData":[OSD([subQ1])],"isStart":false}),makeQuery(id+"F1.opExtrude","SWEPT_FACE",FACE,{"disambiguationData":[OSD([subQ0]),TDD([makeQuery(id+"F0.imprint","IMPRINT",EDGE,{"disambiguationData":[TD([[makeQuery(id+"F0.imprint","INTERSECT",VERTEX,{"derivedFrom":[subQ0,sQuery(id+"F0.wireOp",EDGE,"E20")]}),1.0]])],"derivedFrom":subQ0})])]})],"blendedInto":[makeQuery(id+"F1.opExtrude","SWEPT_FACE",FACE,{"disambiguationData":[OSD([subQ0]),TDD([makeQuery(id+"F0.imprint","IMPRINT",EDGE,{"disambiguationData":[TD([[makeQuery(id+"F0.imprint","INTERSECT",VERTEX,{"derivedFrom":[subQ0,sQuery(id+"F0.wireOp",EDGE,"E20")]}),1.0]])],"derivedFrom":subQ0})])]})]});}
            var Q42;
            {var subQ0=sQuery(id+"F0.wireOp",EDGE,"E20");var subQ1=sQuery(id+"F0.wireOp",EDGE,"E9");Q42=makeQuery(id+"F4.opFillet","BLEND_EDGE",EDGE,{"blendedFrom":[makeQuery(id+"F1.opExtrude","CAP_EDGE",EDGE,{"disambiguationData":[OSD([subQ0])],"isStart":false}),makeQuery(id+"F1.opExtrude","SWEPT_FACE",FACE,{"disambiguationData":[OSD([subQ1]),TDD([makeQuery(id+"F0.imprint","IMPRINT",EDGE,{"disambiguationData":[TD([[makeQuery(id+"F0.imprint","INTERSECT",VERTEX,{"derivedFrom":[subQ1,subQ0]}),1.0]])],"derivedFrom":subQ1})])]})],"blendedInto":[makeQuery(id+"F1.opExtrude","SWEPT_FACE",FACE,{"disambiguationData":[OSD([subQ1]),TDD([makeQuery(id+"F0.imprint","IMPRINT",EDGE,{"disambiguationData":[TD([[makeQuery(id+"F0.imprint","INTERSECT",VERTEX,{"derivedFrom":[subQ1,subQ0]}),1.0]])],"derivedFrom":subQ1})])]})]});}
            var Q43;
            Q43=makeQuery(id+"F1.opExtrude","SWEPT_EDGE",EDGE,{"disambiguationData":[OSD([sQuery(id+"F0.wireOp",EDGE,"E9"),sQuery(id+"F0.wireOp",EDGE,"E21")])]});
            var Q44;
            {var subQ0=sQuery(id+"F0.wireOp",EDGE,"E9");Q44=makeQuery(id+"F1.opExtrude","CAP_EDGE",EDGE,{"disambiguationData":[OSD([subQ0]),TDD([makeQuery(id+"F0.imprint","IMPRINT",EDGE,{"disambiguationData":[TD([[makeQuery(id+"F0.imprint","INTERSECT",VERTEX,{"derivedFrom":[subQ0,sQuery(id+"F0.wireOp",EDGE,"E20")]}),1.0]])],"derivedFrom":subQ0})])],"isStart":true});}
            var Q45;
            {var subQ0=sQuery(id+"F0.wireOp",EDGE,"E9");var subQ1=sQuery(id+"F0.wireOp",EDGE,"E19");Q45=makeQuery(id+"F4.opFillet","BLEND_EDGE",EDGE,{"blendedFrom":[makeQuery(id+"F1.opExtrude","CAP_EDGE",EDGE,{"disambiguationData":[OSD([subQ1])],"isStart":false}),makeQuery(id+"F1.opExtrude","SWEPT_FACE",FACE,{"disambiguationData":[OSD([subQ0]),TDD([makeQuery(id+"F0.imprint","IMPRINT",EDGE,{"disambiguationData":[TD([[makeQuery(id+"F0.imprint","INTERSECT",VERTEX,{"derivedFrom":[subQ0,sQuery(id+"F0.wireOp",EDGE,"E18")]}),1.0]])],"derivedFrom":subQ0})])]})],"blendedInto":[makeQuery(id+"F1.opExtrude","SWEPT_FACE",FACE,{"disambiguationData":[OSD([subQ0]),TDD([makeQuery(id+"F0.imprint","IMPRINT",EDGE,{"disambiguationData":[TD([[makeQuery(id+"F0.imprint","INTERSECT",VERTEX,{"derivedFrom":[subQ0,sQuery(id+"F0.wireOp",EDGE,"E18")]}),1.0]])],"derivedFrom":subQ0})])]})]});}
            var Q46;
            Q46=makeQuery(id+"F1.opExtrude","SWEPT_EDGE",EDGE,{"disambiguationData":[OSD([sQuery(id+"F0.wireOp",EDGE,"E9"),sQuery(id+"F0.wireOp",EDGE,"E20")])]});
            var Q47;
            Q47=makeQuery(id+"F1.opExtrude","SWEPT_EDGE",EDGE,{"disambiguationData":[OSD([sQuery(id+"F0.wireOp",EDGE,"E9"),sQuery(id+"F0.wireOp",EDGE,"E22")])]});
            var Q48;
            {var subQ0=sQuery(id+"F0.wireOp",EDGE,"E9");var subQ1=sQuery(id+"F0.wireOp",EDGE,"E23");Q48=makeQuery(id+"F4.opFillet","BLEND_EDGE",EDGE,{"blendedFrom":[makeQuery(id+"F1.opExtrude","CAP_EDGE",EDGE,{"disambiguationData":[OSD([subQ1])],"isStart":false}),makeQuery(id+"F1.opExtrude","SWEPT_FACE",FACE,{"disambiguationData":[OSD([subQ0]),TDD([makeQuery(id+"F0.imprint","IMPRINT",EDGE,{"disambiguationData":[TD([[makeQuery(id+"F0.imprint","INTERSECT",VERTEX,{"derivedFrom":[subQ0,sQuery(id+"F0.wireOp",EDGE,"E22")]}),1.0]])],"derivedFrom":subQ0})])]})],"blendedInto":[makeQuery(id+"F1.opExtrude","SWEPT_FACE",FACE,{"disambiguationData":[OSD([subQ0]),TDD([makeQuery(id+"F0.imprint","IMPRINT",EDGE,{"disambiguationData":[TD([[makeQuery(id+"F0.imprint","INTERSECT",VERTEX,{"derivedFrom":[subQ0,sQuery(id+"F0.wireOp",EDGE,"E22")]}),1.0]])],"derivedFrom":subQ0})])]})]});}
            var Q49;
            Q49=makeQuery(id+"F1.opExtrude","SWEPT_EDGE",EDGE,{"disambiguationData":[OSD([sQuery(id+"F0.wireOp",EDGE,"E9"),sQuery(id+"F0.wireOp",EDGE,"E23")])]});
            var Q50;
            {var subQ0=sQuery(id+"F0.wireOp",EDGE,"E22");var subQ1=sQuery(id+"F0.wireOp",EDGE,"E9");Q50=makeQuery(id+"F4.opFillet","BLEND_EDGE",EDGE,{"blendedFrom":[makeQuery(id+"F1.opExtrude","CAP_EDGE",EDGE,{"disambiguationData":[OSD([subQ0])],"isStart":false}),makeQuery(id+"F1.opExtrude","SWEPT_FACE",FACE,{"disambiguationData":[OSD([subQ1]),TDD([makeQuery(id+"F0.imprint","IMPRINT",EDGE,{"disambiguationData":[TD([[makeQuery(id+"F0.imprint","INTERSECT",VERTEX,{"derivedFrom":[subQ1,subQ0]}),1.0]])],"derivedFrom":subQ1})])]})],"blendedInto":[makeQuery(id+"F1.opExtrude","SWEPT_FACE",FACE,{"disambiguationData":[OSD([subQ1]),TDD([makeQuery(id+"F0.imprint","IMPRINT",EDGE,{"disambiguationData":[TD([[makeQuery(id+"F0.imprint","INTERSECT",VERTEX,{"derivedFrom":[subQ1,subQ0]}),1.0]])],"derivedFrom":subQ1})])]})]});}
            var Q51;
            {var subQ0=sQuery(id+"F0.wireOp",EDGE,"E9");Q51=makeQuery(id+"F1.opExtrude","CAP_EDGE",EDGE,{"disambiguationData":[OSD([subQ0]),TDD([makeQuery(id+"F0.imprint","IMPRINT",EDGE,{"disambiguationData":[TD([[makeQuery(id+"F0.imprint","INTERSECT",VERTEX,{"derivedFrom":[subQ0,sQuery(id+"F0.wireOp",EDGE,"E22")]}),1.0]])],"derivedFrom":subQ0})])],"isStart":true});}
            var Q52;
            Q52=makeQuery(id+"F1.opExtrude","SWEPT_EDGE",EDGE,{"disambiguationData":[OSD([sQuery(id+"F0.wireOp",EDGE,"E9"),sQuery(id+"F0.wireOp",EDGE,"E24")])]});
            var Q53;
            {var subQ0=sQuery(id+"F0.wireOp",EDGE,"E24");var subQ1=sQuery(id+"F0.wireOp",EDGE,"E9");Q53=makeQuery(id+"F4.opFillet","BLEND_EDGE",EDGE,{"blendedFrom":[makeQuery(id+"F1.opExtrude","CAP_EDGE",EDGE,{"disambiguationData":[OSD([subQ0])],"isStart":false}),makeQuery(id+"F1.opExtrude","SWEPT_FACE",FACE,{"disambiguationData":[OSD([subQ1]),TDD([makeQuery(id+"F0.imprint","IMPRINT",EDGE,{"disambiguationData":[TD([[makeQuery(id+"F0.imprint","INTERSECT",VERTEX,{"derivedFrom":[subQ1,subQ0]}),-1.0]])],"derivedFrom":subQ1})])]})],"blendedInto":[makeQuery(id+"F1.opExtrude","SWEPT_FACE",FACE,{"disambiguationData":[OSD([subQ1]),TDD([makeQuery(id+"F0.imprint","IMPRINT",EDGE,{"disambiguationData":[TD([[makeQuery(id+"F0.imprint","INTERSECT",VERTEX,{"derivedFrom":[subQ1,subQ0]}),-1.0]])],"derivedFrom":subQ1})])]})]});}
            var Q54;
            {var subQ0=sQuery(id+"F0.wireOp",EDGE,"E9");var subQ1=sQuery(id+"F0.wireOp",EDGE,"E33");Q54=makeQuery(id+"F4.opFillet","BLEND_EDGE",EDGE,{"blendedFrom":[makeQuery(id+"F1.opExtrude","CAP_EDGE",EDGE,{"disambiguationData":[OSD([subQ1])],"isStart":false}),makeQuery(id+"F1.opExtrude","SWEPT_FACE",FACE,{"disambiguationData":[OSD([subQ0]),TDD([makeQuery(id+"F0.imprint","IMPRINT",EDGE,{"disambiguationData":[TD([[makeQuery(id+"F0.imprint","INTERSECT",VERTEX,{"derivedFrom":[subQ0,sQuery(id+"F0.wireOp",EDGE,"E24")]}),-1.0]])],"derivedFrom":subQ0})])]})],"blendedInto":[makeQuery(id+"F1.opExtrude","SWEPT_FACE",FACE,{"disambiguationData":[OSD([subQ0]),TDD([makeQuery(id+"F0.imprint","IMPRINT",EDGE,{"disambiguationData":[TD([[makeQuery(id+"F0.imprint","INTERSECT",VERTEX,{"derivedFrom":[subQ0,sQuery(id+"F0.wireOp",EDGE,"E24")]}),-1.0]])],"derivedFrom":subQ0})])]})]});}
            var Q55;
            Q55=makeQuery(id+"F1.opExtrude","SWEPT_EDGE",EDGE,{"disambiguationData":[OSD([sQuery(id+"F0.wireOp",EDGE,"E9"),sQuery(id+"F0.wireOp",EDGE,"E33")])]});
            var Q56;
            {var subQ0=sQuery(id+"F0.wireOp",EDGE,"E9");Q56=makeQuery(id+"F1.opExtrude","CAP_EDGE",EDGE,{"disambiguationData":[OSD([subQ0]),TDD([makeQuery(id+"F0.imprint","IMPRINT",EDGE,{"disambiguationData":[TD([[makeQuery(id+"F0.imprint","INTERSECT",VERTEX,{"derivedFrom":[subQ0,sQuery(id+"F0.wireOp",EDGE,"E24")]}),-1.0]])],"derivedFrom":subQ0})])],"isStart":true});}
            var Q57;
            Q57=makeQuery(id+"F1.opExtrude","SWEPT_EDGE",EDGE,{"disambiguationData":[OSD([sQuery(id+"F0.wireOp",EDGE,"E15"),sQuery(id+"F0.wireOp",EDGE,"E31.trimOffspring")])]});
            var Q58;
            Q58=makeQuery(id+"F1.opExtrude","SWEPT_EDGE",EDGE,{"disambiguationData":[OSD([sQuery(id+"F0.wireOp",EDGE,"E15"),sQuery(id+"F0.wireOp",EDGE,"E30.trimOffspring")])]});
            var Q59;
            Q59=makeQuery(id+"F1.opExtrude","SWEPT_EDGE",EDGE,{"disambiguationData":[OSD([sQuery(id+"F0.wireOp",EDGE,"E15"),sQuery(id+"F0.wireOp",EDGE,"E34.trimOffspring")])]});
            var Q60;
            {var subQ0=sQuery(id+"F0.wireOp",EDGE,"E30.trimOffspring");var subQ1=sQuery(id+"F0.wireOp",EDGE,"E15");Q60=makeQuery(id+"F4.opFillet","BLEND_EDGE",EDGE,{"blendedFrom":[makeQuery(id+"F1.opExtrude","CAP_EDGE",EDGE,{"disambiguationData":[OSD([subQ0])],"isStart":false}),makeQuery(id+"F1.opExtrude","SWEPT_FACE",FACE,{"disambiguationData":[OSD([subQ1]),TDD([makeQuery(id+"F0.imprint","IMPRINT",EDGE,{"disambiguationData":[TD([[makeQuery(id+"F0.imprint","INTERSECT",VERTEX,{"derivedFrom":[subQ1,subQ0]}),-1.0]])],"derivedFrom":subQ1})])]})],"blendedInto":[makeQuery(id+"F1.opExtrude","SWEPT_FACE",FACE,{"disambiguationData":[OSD([subQ1]),TDD([makeQuery(id+"F0.imprint","IMPRINT",EDGE,{"disambiguationData":[TD([[makeQuery(id+"F0.imprint","INTERSECT",VERTEX,{"derivedFrom":[subQ1,subQ0]}),-1.0]])],"derivedFrom":subQ1})])]})]});}
            var Q61;
            Q61=makeQuery(id+"F1.opExtrude","SWEPT_EDGE",EDGE,{"disambiguationData":[OSD([sQuery(id+"F0.wireOp",EDGE,"E15"),sQuery(id+"F0.wireOp",EDGE,"E29.trimOffspring")])]});
            var Q62;
            {var subQ0=sQuery(id+"F0.wireOp",EDGE,"E15");var subQ1=sQuery(id+"F0.wireOp",EDGE,"E34.trimOffspring");Q62=makeQuery(id+"F4.opFillet","BLEND_EDGE",EDGE,{"blendedFrom":[makeQuery(id+"F1.opExtrude","CAP_EDGE",EDGE,{"disambiguationData":[OSD([subQ1])],"isStart":false}),makeQuery(id+"F1.opExtrude","SWEPT_FACE",FACE,{"disambiguationData":[OSD([subQ0]),TDD([makeQuery(id+"F0.imprint","IMPRINT",EDGE,{"disambiguationData":[TD([[makeQuery(id+"F0.imprint","INTERSECT",VERTEX,{"derivedFrom":[subQ0,sQuery(id+"F0.wireOp",EDGE,"E29.trimOffspring")]}),-1.0]])],"derivedFrom":subQ0})])]})],"blendedInto":[makeQuery(id+"F1.opExtrude","SWEPT_FACE",FACE,{"disambiguationData":[OSD([subQ0]),TDD([makeQuery(id+"F0.imprint","IMPRINT",EDGE,{"disambiguationData":[TD([[makeQuery(id+"F0.imprint","INTERSECT",VERTEX,{"derivedFrom":[subQ0,sQuery(id+"F0.wireOp",EDGE,"E29.trimOffspring")]}),-1.0]])],"derivedFrom":subQ0})])]})]});}
            var Q63;
            Q63=makeQuery(id+"F1.opExtrude","SWEPT_EDGE",EDGE,{"disambiguationData":[OSD([sQuery(id+"F0.wireOp",EDGE,"E14"),sQuery(id+"F0.wireOp",EDGE,"E24")])]});
            var Q64;
            Q64=makeQuery(id+"F4.opFillet","BLEND_FACE",FACE,{"disambiguationData":[OSD([sQuery(id+"F0.wireOp",EDGE,"E24")])]});
            var Q65;
            Q65=makeQuery(id+"F1.opExtrude","SWEPT_EDGE",EDGE,{"disambiguationData":[OSD([sQuery(id+"F0.wireOp",EDGE,"E14"),sQuery(id+"F0.wireOp",EDGE,"E23")])]});
            var Q66;
            {var subQ0=sQuery(id+"F0.wireOp",EDGE,"E14");var subQ1=sQuery(id+"F0.wireOp",EDGE,"E23");Q66=makeQuery(id+"F4.opFillet","BLEND_EDGE",EDGE,{"blendedFrom":[makeQuery(id+"F1.opExtrude","CAP_EDGE",EDGE,{"disambiguationData":[OSD([subQ1])],"isStart":false}),makeQuery(id+"F1.opExtrude","SWEPT_FACE",FACE,{"disambiguationData":[OSD([subQ0]),TDD([makeQuery(id+"F0.imprint","IMPRINT",EDGE,{"disambiguationData":[TD([[makeQuery(id+"F0.imprint","INTERSECT",VERTEX,{"derivedFrom":[subQ0,sQuery(id+"F0.wireOp",EDGE,"E22")]}),1.0]])],"derivedFrom":subQ0})])]})],"blendedInto":[makeQuery(id+"F1.opExtrude","SWEPT_FACE",FACE,{"disambiguationData":[OSD([subQ0]),TDD([makeQuery(id+"F0.imprint","IMPRINT",EDGE,{"disambiguationData":[TD([[makeQuery(id+"F0.imprint","INTERSECT",VERTEX,{"derivedFrom":[subQ0,sQuery(id+"F0.wireOp",EDGE,"E22")]}),1.0]])],"derivedFrom":subQ0})])]})]});}
            var Q67;
            {var subQ0=sQuery(id+"F0.wireOp",EDGE,"E22");var subQ1=sQuery(id+"F0.wireOp",EDGE,"E14");Q67=makeQuery(id+"F4.opFillet","BLEND_EDGE",EDGE,{"blendedFrom":[makeQuery(id+"F1.opExtrude","CAP_EDGE",EDGE,{"disambiguationData":[OSD([subQ0])],"isStart":false}),makeQuery(id+"F1.opExtrude","SWEPT_FACE",FACE,{"disambiguationData":[OSD([subQ1]),TDD([makeQuery(id+"F0.imprint","IMPRINT",EDGE,{"disambiguationData":[TD([[makeQuery(id+"F0.imprint","INTERSECT",VERTEX,{"derivedFrom":[subQ1,subQ0]}),1.0]])],"derivedFrom":subQ1})])]})],"blendedInto":[makeQuery(id+"F1.opExtrude","SWEPT_FACE",FACE,{"disambiguationData":[OSD([subQ1]),TDD([makeQuery(id+"F0.imprint","IMPRINT",EDGE,{"disambiguationData":[TD([[makeQuery(id+"F0.imprint","INTERSECT",VERTEX,{"derivedFrom":[subQ1,subQ0]}),1.0]])],"derivedFrom":subQ1})])]})]});}
            var Q68;
            Q68=makeQuery(id+"F1.opExtrude","SWEPT_EDGE",EDGE,{"disambiguationData":[OSD([sQuery(id+"F0.wireOp",EDGE,"E14"),sQuery(id+"F0.wireOp",EDGE,"E22")])]});
            var Q69;
            {var subQ0=sQuery(id+"F0.wireOp",EDGE,"E14");var subQ1=sQuery(id+"F0.wireOp",EDGE,"E33");Q69=makeQuery(id+"F4.opFillet","BLEND_EDGE",EDGE,{"blendedFrom":[makeQuery(id+"F1.opExtrude","CAP_EDGE",EDGE,{"disambiguationData":[OSD([subQ1])],"isStart":false}),makeQuery(id+"F1.opExtrude","SWEPT_FACE",FACE,{"disambiguationData":[OSD([subQ0]),TDD([makeQuery(id+"F0.imprint","IMPRINT",EDGE,{"disambiguationData":[TD([[makeQuery(id+"F0.imprint","INTERSECT",VERTEX,{"derivedFrom":[subQ0,sQuery(id+"F0.wireOp",EDGE,"E24")]}),-1.0]])],"derivedFrom":subQ0})])]})],"blendedInto":[makeQuery(id+"F1.opExtrude","SWEPT_FACE",FACE,{"disambiguationData":[OSD([subQ0]),TDD([makeQuery(id+"F0.imprint","IMPRINT",EDGE,{"disambiguationData":[TD([[makeQuery(id+"F0.imprint","INTERSECT",VERTEX,{"derivedFrom":[subQ0,sQuery(id+"F0.wireOp",EDGE,"E24")]}),-1.0]])],"derivedFrom":subQ0})])]})]});}
            var Q70;
            Q70=makeQuery(id+"F1.opExtrude","SWEPT_EDGE",EDGE,{"disambiguationData":[OSD([sQuery(id+"F0.wireOp",EDGE,"E14"),sQuery(id+"F0.wireOp",EDGE,"E33")])]});
            fillet(context, id + "F6", {"entities" : qUnion([Q0, Q1, Q2, Q3, Q4, Q5, Q6, Q7, Q8, Q9, Q10, Q11, Q12, Q13, Q14, Q15, Q16, Q17, Q18, Q19, Q20, Q21, Q22, Q23, Q24, Q25, Q26, Q27, Q28, Q29, Q30, Q31, Q32, Q33, Q34, Q35, Q36, Q37, Q38, Q39, Q40, Q41, Q42, Q43, Q44, Q45, Q46, Q47, Q48, Q49, Q50, Q51, Q52, Q53, Q54, Q55, Q56, Q57, Q58, Q59, Q60, Q61, Q62, Q63, Q64, Q65, Q66, Q67, Q68, Q69, Q70]), "radius" : 0.5 * mm, "tangentPropagation" : true, "allowEdgeOverflow" : false});
        }
        {
            var Q0;
            Q0=makeQuery(id+"F2.imprint","IMPRINT",FACE,{"disambiguationData":[TD([[makeQuery(id+"F2.imprint","IMPRINT",EDGE,{"derivedFrom":sQuery(id+"F2.wireOp",EDGE,"E38")}),-1.0]])]});
            extrude(context, id + "F7", {"entities" : qUnion([Q0]), "oppositeDirection" : true, "depth" : 3.17 * mm, "offsetDistance" : 25.4 * mm});
        }
        {
            var Q0;
            {var subQ0=sQuery(id+"F0.wireOp",EDGE,"E14");Q0=makeQuery(id+"F1.opExtrude","CAP_EDGE",EDGE,{"disambiguationData":[OSD([subQ0]),TDD([makeQuery(id+"F0.imprint","IMPRINT",EDGE,{"disambiguationData":[TD([[makeQuery(id+"F0.imprint","INTERSECT",VERTEX,{"derivedFrom":[subQ0,sQuery(id+"F0.wireOp",EDGE,"E26")]}),-1.0]])],"derivedFrom":subQ0})])],"isStart":true});}
            var Q1;
            Q1=makeQuery(id+"F1.opExtrude","CAP_EDGE",EDGE,{"disambiguationData":[OSD([sQuery(id+"F0.wireOp",EDGE,"E26")])],"isStart":true});
            var Q2;
            {var subQ0=sQuery(id+"F0.wireOp",EDGE,"E15");Q2=makeQuery(id+"F1.opExtrude","CAP_EDGE",EDGE,{"disambiguationData":[OSD([subQ0]),TDD([makeQuery(id+"F0.imprint","IMPRINT",EDGE,{"disambiguationData":[TD([[makeQuery(id+"F0.imprint","INTERSECT",VERTEX,{"derivedFrom":[subQ0,sQuery(id+"F0.wireOp",EDGE,"E26")]}),-1.0]])],"derivedFrom":subQ0})])],"isStart":true});}
            var Q3;
            Q3=makeQuery(id+"F7.opExtrude","CAP_EDGE",EDGE,{"disambiguationData":[OSD([sQuery(id+"F2.wireOp",EDGE,"E40"),sQuery(id+"F2.wireOp",EDGE,"E43")])],"isStart":true});
            var Q4;
            Q4=makeQuery(id+"F7.opExtrude","CAP_EDGE",EDGE,{"disambiguationData":[OSD([sQuery(id+"F2.wireOp",EDGE,"E41"),sQuery(id+"F2.wireOp",EDGE,"E45")])],"isStart":true});
            fillet(context, id + "F8", {"entities" : qUnion([Q0, Q1, Q2, Q3, Q4]), "radius" : 3.17 * mm, "tangentPropagation" : true, "allowEdgeOverflow" : false});
        }
        {
            var Q0;
            Q0=makeQuery(id+"F7.opExtrude","CAP_EDGE",EDGE,{"disambiguationData":[OSD([sQuery(id+"F2.wireOp",EDGE,"E38")])],"isStart":true});
            var Q1;
            Q1=makeQuery(id+"F7.opExtrude","CAP_EDGE",EDGE,{"disambiguationData":[OSD([sQuery(id+"F2.wireOp",EDGE,"E37")])],"isStart":true});
            fillet(context, id + "F9", {"entities" : qUnion([Q0, Q1]), "radius" : 2.54 * mm, "tangentPropagation" : true, "allowEdgeOverflow" : false});
        }
        {
            var Q0;
            {var subQ0=sQuery(id+"F0.wireOp",EDGE,"E2");Q0=makeQuery(id+"F1.opExtrude","CAP_EDGE",EDGE,{"disambiguationData":[OSD([subQ0]),TDD([makeQuery(id+"F0.imprint","IMPRINT",EDGE,{"disambiguationData":[TD([[makeQuery(id+"F0.imprint","INTERSECT",VERTEX,{"derivedFrom":[subQ0,sQuery(id+"F0.wireOp",EDGE,"E3")]}),1.0]])],"derivedFrom":subQ0})])],"isStart":true});}
            var Q1;
            {var subQ0=sQuery(id+"F0.wireOp",EDGE,"E17");var subQ1=sQuery(id+"F0.wireOp",EDGE,"E2");Q1=makeQuery(id+"FveVwo7CrqcUzTx_9.opFillet","BLEND_EDGE",EDGE,{"blendedFrom":[makeQuery(id+"F1.opExtrude","SWEPT_EDGE",EDGE,{"disambiguationData":[OSD([subQ1,subQ0])]}),makeQuery(id+"F1.opExtrude","CAP_FACE",FACE,{"disambiguationData":[OSD([subQ1,sQuery(id+"F0.wireOp",EDGE,"E3"),sQuery(id+"F0.wireOp",EDGE,"E9"),sQuery(id+"F0.wireOp",EDGE,"E10"),sQuery(id+"F0.wireOp",EDGE,"E11"),sQuery(id+"F0.wireOp",EDGE,"E12"),sQuery(id+"F0.wireOp",EDGE,"E13.filletArc"),subQ0])],"isStart":true})],"blendedInto":[makeQuery(id+"F1.opExtrude","CAP_FACE",FACE,{"disambiguationData":[OSD([subQ1,sQuery(id+"F0.wireOp",EDGE,"E3"),sQuery(id+"F0.wireOp",EDGE,"E9"),sQuery(id+"F0.wireOp",EDGE,"E10"),sQuery(id+"F0.wireOp",EDGE,"E11"),sQuery(id+"F0.wireOp",EDGE,"E12"),sQuery(id+"F0.wireOp",EDGE,"E13.filletArc"),subQ0])],"isStart":true})]});}
            var Q2;
            {var subQ0=sQuery(id+"F0.wireOp",EDGE,"E17");Q2=makeQuery(id+"FveVwo7CrqcUzTx_9.opFillet","BLEND_EDGE",EDGE,{"blendedFrom":[makeQuery(id+"F1.opExtrude","SWEPT_EDGE",EDGE,{"disambiguationData":[OSD([sQuery(id+"F0.wireOp",EDGE,"E2"),subQ0])]}),makeQuery(id+"F1.opExtrude","CAP_EDGE",EDGE,{"disambiguationData":[OSD([subQ0])],"isStart":true})],"blendedInto":[]});}
            fillet(context, id + "F10", {"entities" : qUnion([Q0, Q1, Q2]), "radius" : 2.54 * mm, "tangentPropagation" : true, "allowEdgeOverflow" : false});
        }
        {
            var Q0;
            {var subQ0=sQuery(id+"F0.wireOp",EDGE,"E28.trimOffspring");var subQ1=sQuery(id+"F0.wireOp",EDGE,"E2");Q0=makeQuery(id+"F3.opFillet","BLEND_EDGE",EDGE,{"blendedFrom":[makeQuery(id+"F1.opExtrude","CAP_EDGE",EDGE,{"disambiguationData":[OSD([subQ1]),TDD([makeQuery(id+"F0.imprint","IMPRINT",EDGE,{"disambiguationData":[TD([[makeQuery(id+"F0.imprint","INTERSECT",VERTEX,{"derivedFrom":[subQ1,sQuery(id+"F0.wireOp",EDGE,"E6.filletArc")]}),-1.0]])],"derivedFrom":subQ1})])],"isStart":true}),makeQuery(id+"F1.opExtrude","SWEPT_FACE",FACE,{"disambiguationData":[OSD([subQ0])]})],"blendedInto":[makeQuery(id+"F1.opExtrude","SWEPT_FACE",FACE,{"disambiguationData":[OSD([subQ0])]})]});}
            var Q1;
            Q1=makeQuery(id+"F3.opFillet","BLEND_EDGE",EDGE,{"blendedFrom":[makeQuery(id+"F1.opExtrude","CAP_EDGE",EDGE,{"disambiguationData":[OSD([sQuery(id+"F0.wireOp",EDGE,"E35")])],"isStart":true}),makeQuery(id+"F1.opExtrude","SWEPT_FACE",FACE,{"disambiguationData":[OSD([sQuery(id+"F0.wireOp",EDGE,"E25")])]})],"blendedInto":[makeQuery(id+"F1.opExtrude","SWEPT_FACE",FACE,{"disambiguationData":[OSD([sQuery(id+"F0.wireOp",EDGE,"E25")])]})]});
            fillet(context, id + "F11", {"entities" : qUnion([Q0, Q1]), "radius" : 0.25 * mm, "tangentPropagation" : true, "allowEdgeOverflow" : false});
        }
        {
            var Q0;
            Q0=qCreatedBy(makeId("Front.planeOp"),FACE);
            var sketch = newSketch(context, id + "F12", { "sketchPlane" : qUnion([Q0])});
            skPoint(sketch, "E46.visualSharp", {"position": v(14.98, 161.49) * mm});
            skLineSegment(sketch, "E47", {"start": v(31.93, -20.11) * mm, "end": v(31.93, 121.37) * mm});
            skLineSegment(sketch, "E48", {"start": v(17.3, -20.11) * mm, "end": v(17.3, 144.43) * mm});
            skPoint(sketch, "E49.visualSharp", {"position": v(17.3, 156.28) * mm});
            skArc(sketch, "E49.filletArc", {"start": v(17.3, 144.43) * mm, "mid": v(13.94, 157.07) * mm, "end": v(4.73, 166.36) * mm});
            skLineSegment(sketch, "E50", {"start": v(4.73, 166.36) * mm, "end": v(-0.55, 169.45) * mm});
            skLineSegment(sketch, "E51", {"start": v(31.93, 121.37) * mm, "end": v(31.93, 162.28) * mm});
            skLineSegment(sketch, "E52", {"start": v(17.12, 209.8) * mm, "end": v(17.12, 261.76) * mm});
            skPoint(sketch, "E53.visualSharp", {"position": v(31.93, 166.36) * mm});
            skPoint(sketch, "E54.visualSharp", {"position": v(17.12, 199.36) * mm});
            skArc(sketch, "E55", {"start": v(31.93, 162.28) * mm, "mid": v(29, 181.5) * mm, "end": v(20.5, 198.98) * mm});
            skPoint(sketch, "E56.visualSharp", {"position": v(17.12, 203.44) * mm});
            skArc(sketch, "E56.filletArc", {"start": v(17.12, 209.8) * mm, "mid": v(17.98, 204.14) * mm, "end": v(20.5, 198.98) * mm});
            skLineSegment(sketch, "E57", {"start": v(17.12, 261.76) * mm, "end": v(14, 261.76) * mm});
            skPoint(sketch, "E58.orphan", {"position": v(17.12, 271.5) * mm});
            skPoint(sketch, "E59.orphan", {"position": v(-1.84, 271.5) * mm});
            skLineSegment(sketch, "E60", {"start": v(-0.55, 169.45) * mm, "end": v(-1.37, 169.93) * mm});
            skLineSegment(sketch, "E61", {"start": v(-2.94, 172.67) * mm, "end": v(-2.94, 231.39) * mm});
            skArc(sketch, "E62", {"start": v(14, 261.76) * mm, "mid": v(1.58, 248.78) * mm, "end": v(-2.94, 231.39) * mm});
            skArc(sketch, "E63", {"start": v(17.3, -20.11) * mm, "mid": v(24.62, -27.43) * mm, "end": v(31.93, -20.11) * mm});
            skPoint(sketch, "E64.visualSharp", {"position": v(-2.94, 170.85) * mm});
            skArc(sketch, "E64.filletArc", {"start": v(-2.94, 171.26) * mm, "mid": v(-2.85, 170.9) * mm, "end": v(-2.59, 170.64) * mm});
            skArc(sketch, "E65.filletArc", {"start": v(-2.94, 172.67) * mm, "mid": v(-2.52, 171.09) * mm, "end": v(-1.37, 169.93) * mm});
            skSolve(sketch);
        }
        {
            var Q0;
            Q0=makeQuery(id+"F12.imprint","IMPRINT",FACE,{"disambiguationData":[TD([[makeQuery(id+"F12.imprint","IMPRINT",EDGE,{"derivedFrom":sQuery(id+"F12.wireOp",EDGE,"E47")}),1.0]])]});
            extrude(context, id + "F13", {"entities" : qUnion([Q0]), "depth" : 6.35 * mm, "offsetDistance" : 25.4 * mm});
        }
        {
            var Q0;
            Q0=makeQuery(id+"F13.opExtrude","CAP_FACE",FACE,{"disambiguationData":[OSD([sQuery(id+"F12.wireOp",EDGE,"E47"),sQuery(id+"F12.wireOp",EDGE,"E48"),sQuery(id+"F12.wireOp",EDGE,"E49.filletArc"),sQuery(id+"F12.wireOp",EDGE,"E50"),sQuery(id+"F12.wireOp",EDGE,"E51"),sQuery(id+"F12.wireOp",EDGE,"E52"),sQuery(id+"F12.wireOp",EDGE,"E55"),sQuery(id+"F12.wireOp",EDGE,"E56.filletArc"),sQuery(id+"F12.wireOp",EDGE,"E57"),sQuery(id+"F12.wireOp",EDGE,"E60"),sQuery(id+"F12.wireOp",EDGE,"E61"),sQuery(id+"F12.wireOp",EDGE,"E62"),sQuery(id+"F12.wireOp",EDGE,"E63"),sQuery(id+"F12.wireOp",EDGE,"E65.filletArc")])],"isStart":true});
            var sketch = newSketch(context, id + "F14", { "sketchPlane" : qUnion([Q0])});
            skSolve(sketch);
        }
        {
            var Q0;
            Q0=makeQuery(id+"F14.imprint","IMPRINT",FACE,{"disambiguationData":[TD([[makeQuery(id+"F14.imprint","IMPRINT",EDGE,{"derivedFrom":makeQuery(id+"F13.opExtrude","CAP_EDGE",EDGE,{"disambiguationData":[OSD([sQuery(id+"F12.wireOp",EDGE,"E48")])],"isStart":true})}),1.0]])]});
            extrude(context, id + "F15", {"entities" : qUnion([Q0]), "oppositeDirection" : true, "depth" : 6.35 * mm, "offsetDistance" : 25.4 * mm});
        }
    });
